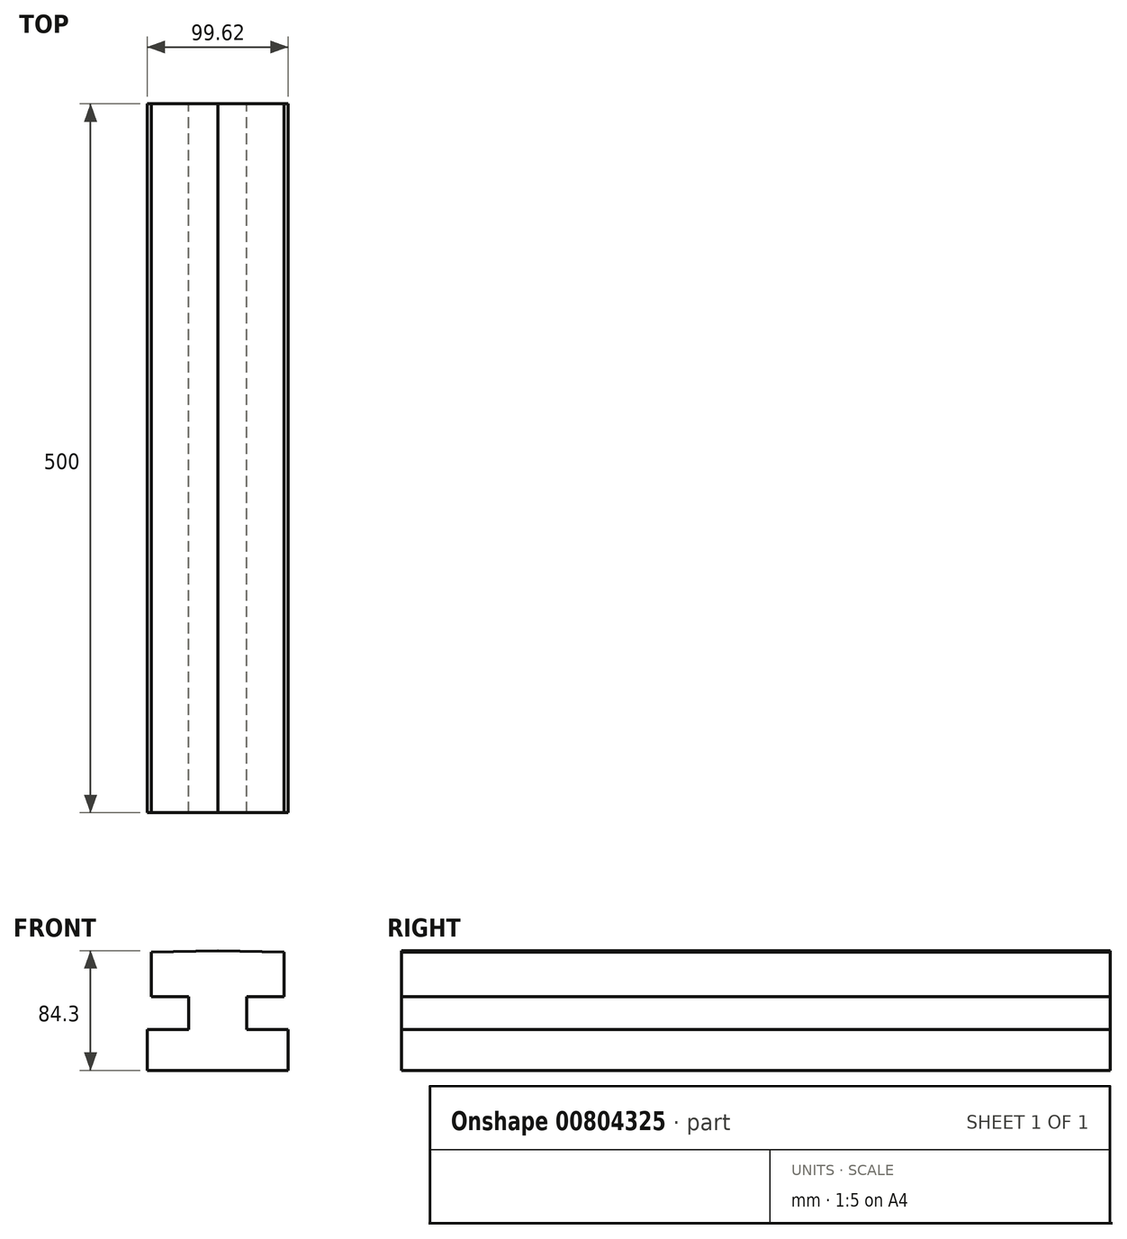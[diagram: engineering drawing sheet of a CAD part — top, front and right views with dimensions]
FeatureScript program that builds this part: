
annotation { "Feature Type Name" : "Feature", "Feature Type Description" : "" }
export const myFeature = defineFeature(function(context is Context, id is Id, definition is map)
    precondition{}
    {
        {
            var Q0;
            Q0=qCreatedBy(makeId("Front.planeOp"),FACE);
            var sketch = newSketch(context, id + "F0", { "sketchPlane" : qUnion([Q0])});
            skLineSegment(sketch, "E0", {"start": v(0, 45.32) * mm, "end": v(0, -38.98) * mm, "construction": true});
            skLineSegment(sketch, "E1", {"start": v(0, -38.98) * mm, "end": v(49.81, -38.98) * mm});
            skLineSegment(sketch, "E2", {"start": v(49.81, -38.98) * mm, "end": v(49.81, -10.17) * mm});
            skLineSegment(sketch, "E3", {"start": v(49.81, -10.17) * mm, "end": v(20.48, -10.17) * mm});
            skLineSegment(sketch, "E4", {"start": v(20.48, -10.17) * mm, "end": v(20.48, 12.82) * mm});
            skLineSegment(sketch, "E5", {"start": v(20.48, 12.82) * mm, "end": v(46.9, 12.82) * mm});
            skLineSegment(sketch, "E6", {"start": v(46.9, 12.82) * mm, "end": v(46.9, 44.26) * mm});
            skLineSegment(sketch, "E7", {"start": v(46.9, 44.26) * mm, "end": v(0, 45.32) * mm});
            skLineSegment(sketch, "E8.MirrorCS", {"start": v(-46.9, 44.26) * mm, "end": v(0, 45.32) * mm});
            skLineSegment(sketch, "E9.MirrorCS", {"start": v(-46.9, 12.82) * mm, "end": v(-46.9, 44.26) * mm});
            skLineSegment(sketch, "E10.MirrorCS", {"start": v(-20.48, 12.82) * mm, "end": v(-46.9, 12.82) * mm});
            skLineSegment(sketch, "E11.MirrorCS", {"start": v(-20.48, -10.17) * mm, "end": v(-20.48, 12.82) * mm});
            skLineSegment(sketch, "E12.MirrorCS", {"start": v(-49.81, -10.17) * mm, "end": v(-20.48, -10.17) * mm});
            skLineSegment(sketch, "E13.MirrorCS", {"start": v(-49.81, -38.98) * mm, "end": v(-49.81, -10.17) * mm});
            skLineSegment(sketch, "E14.MirrorCS", {"start": v(0, -38.98) * mm, "end": v(-49.81, -38.98) * mm});
            skSolve(sketch);
        }
        {
            var Q0;
            Q0=qSketchRegion(id+"F0",true);
            extrude(context, id + "F1", {"entities" : qUnion([Q0]), "depth" : 500 * mm, "offsetDistance" : 25 * mm});
        }
    });
